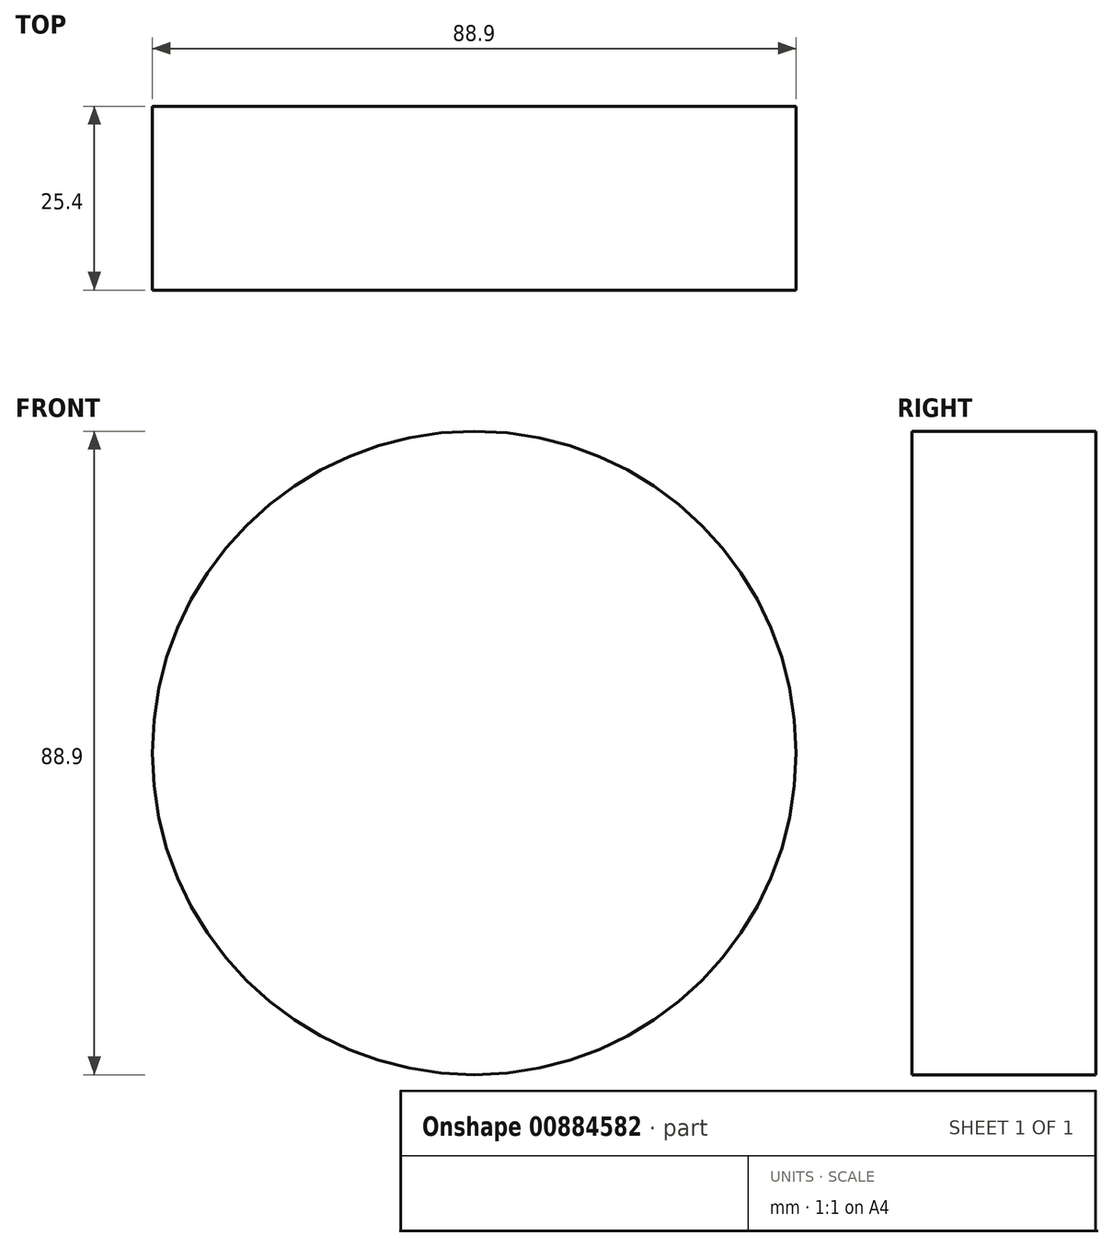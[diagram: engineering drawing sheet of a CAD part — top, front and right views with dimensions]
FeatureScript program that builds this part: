
annotation { "Feature Type Name" : "Feature", "Feature Type Description" : "" }
export const myFeature = defineFeature(function(context is Context, id is Id, definition is map)
    precondition{}
    {
        {
            var Q0;
            Q0=qCreatedBy(makeId("Front.planeOp"),FACE);
            var sketch = newSketch(context, id + "F0", { "sketchPlane" : qUnion([Q0])});
            skCircle(sketch, "E0", {"center": v(0, 0) * mm, "radius": 44.45 * mm});
            skSolve(sketch);
        }
        {
            var Q0;
            Q0=makeQuery(id+"F0.imprint","IMPRINT",FACE,{"disambiguationData":[TD([[makeQuery(id+"F0.imprint","IMPRINT",EDGE,{"derivedFrom":sQuery(id+"F0.wireOp",EDGE,"E0")}),1.0]])]});
            extrude(context, id + "F1", {"entities" : qUnion([Q0]), "depth" : 25.4 * mm, "offsetDistance" : 25.4 * mm});
        }
    });
